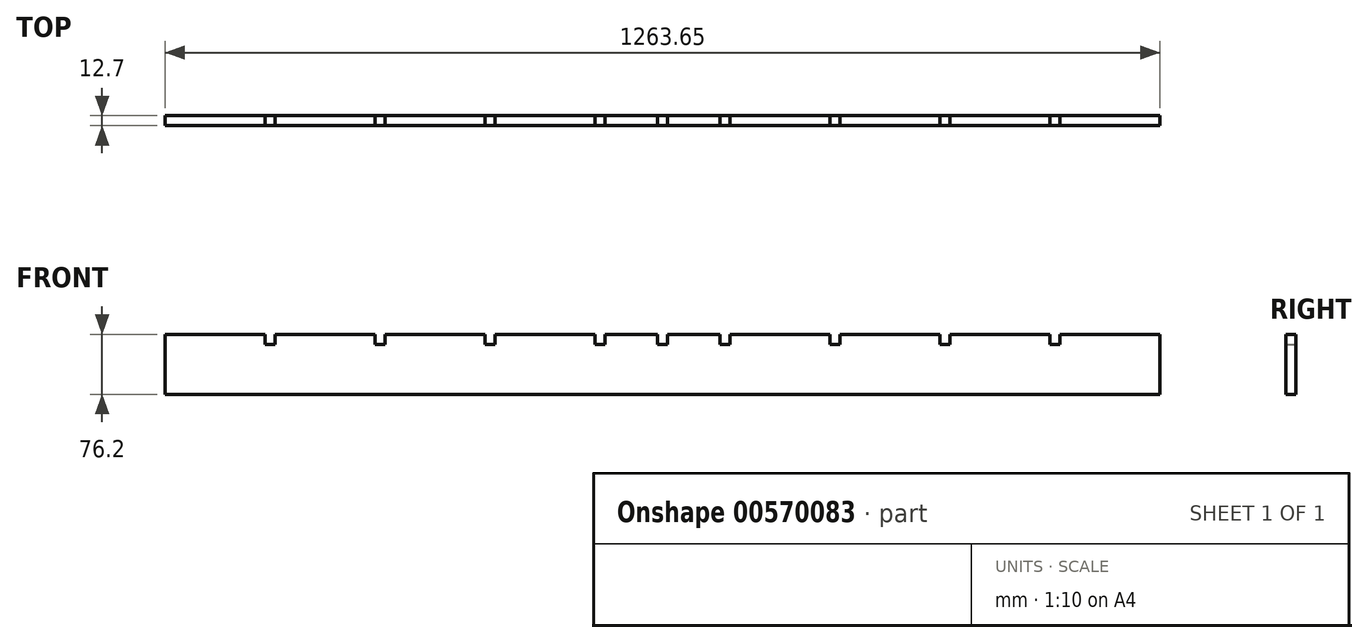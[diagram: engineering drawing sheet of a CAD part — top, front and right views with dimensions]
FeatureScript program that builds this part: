
annotation { "Feature Type Name" : "Feature", "Feature Type Description" : "" }
export const myFeature = defineFeature(function(context is Context, id is Id, definition is map)
    precondition{}
    {
        {
            var Q0;
            Q0=qCreatedBy(makeId("Right.planeOp"),FACE);
            var sketch = newSketch(context, id + "F0", { "sketchPlane" : qUnion([Q0])});
            skLineSegment(sketch, "E0", {"start": v(0, 0) * mm, "end": v(12.7, 0) * mm});
            skLineSegment(sketch, "E1", {"start": v(12.7, 0) * mm, "end": v(12.7, 76.2) * mm});
            skLineSegment(sketch, "E2", {"start": v(12.7, 76.2) * mm, "end": v(0, 76.2) * mm});
            skLineSegment(sketch, "E3", {"start": v(0, 76.2) * mm, "end": v(0, 0) * mm});
            skSolve(sketch);
        }
        {
            var Q0;
            Q0 = qSketchRegion(id + "F0", true);
            extrude(context, id + "F1", {"entities" : qUnion([Q0]), "oppositeDirection" : true, "depth" : 1263.65 * mm, "offsetDistance" : 25.4 * mm});
        }
        {
            var Q0;
            Q0=makeQuery(id+"F1.opExtrude","SWEPT_FACE",FACE,{"disambiguationData":[OSD([sQuery(id+"F0.wireOp",EDGE,"E1")])]});
            var sketch = newSketch(context, id + "F2", { "sketchPlane" : qUnion([Q0])});
            skLineSegment(sketch, "E4", {"start": v(127, 76.2) * mm, "end": v(127, 63.5) * mm});
            skLineSegment(sketch, "E5", {"start": v(127, 63.5) * mm, "end": v(139.7, 63.5) * mm});
            skLineSegment(sketch, "E6", {"start": v(139.7, 63.5) * mm, "end": v(139.7, 76.2) * mm});
            skLineSegment(sketch, "E7", {"start": v(1136.65, 76.2) * mm, "end": v(1136.65, 63.5) * mm});
            skLineSegment(sketch, "E8", {"start": v(1136.65, 63.5) * mm, "end": v(1123.95, 63.5) * mm});
            skLineSegment(sketch, "E9", {"start": v(1123.95, 63.5) * mm, "end": v(1123.95, 76.2) * mm});
            skLineSegment(sketch, "E10", {"start": v(996.95, 76.2) * mm, "end": v(996.95, 63.5) * mm});
            skLineSegment(sketch, "E11", {"start": v(996.95, 63.5) * mm, "end": v(984.25, 63.5) * mm});
            skLineSegment(sketch, "E12", {"start": v(984.25, 63.5) * mm, "end": v(984.25, 76.2) * mm});
            skLineSegment(sketch, "E13", {"start": v(266.7, 76.2) * mm, "end": v(266.7, 63.5) * mm});
            skLineSegment(sketch, "E14", {"start": v(266.7, 63.5) * mm, "end": v(279.4, 63.5) * mm});
            skLineSegment(sketch, "E15", {"start": v(279.4, 63.5) * mm, "end": v(279.4, 76.2) * mm});
            skLineSegment(sketch, "E16", {"start": v(406.4, 76.2) * mm, "end": v(406.4, 63.5) * mm});
            skLineSegment(sketch, "E17", {"start": v(406.4, 63.5) * mm, "end": v(419.1, 63.5) * mm});
            skLineSegment(sketch, "E18", {"start": v(419.1, 63.5) * mm, "end": v(419.1, 76.2) * mm});
            skLineSegment(sketch, "E19", {"start": v(857.25, 76.2) * mm, "end": v(857.25, 63.5) * mm});
            skLineSegment(sketch, "E20", {"start": v(857.25, 63.5) * mm, "end": v(844.55, 63.5) * mm});
            skLineSegment(sketch, "E21", {"start": v(844.55, 63.5) * mm, "end": v(844.55, 76.2) * mm});
            skLineSegment(sketch, "E22", {"start": v(546.1, 76.2) * mm, "end": v(546.1, 63.5) * mm});
            skLineSegment(sketch, "E23", {"start": v(546.1, 63.5) * mm, "end": v(558.8, 63.5) * mm});
            skLineSegment(sketch, "E24", {"start": v(558.8, 63.5) * mm, "end": v(558.8, 76.2) * mm});
            skLineSegment(sketch, "E25", {"start": v(717.55, 76.2) * mm, "end": v(717.55, 63.5) * mm});
            skLineSegment(sketch, "E26", {"start": v(717.55, 63.5) * mm, "end": v(704.85, 63.5) * mm});
            skLineSegment(sketch, "E27", {"start": v(704.85, 63.5) * mm, "end": v(704.85, 76.2) * mm});
            skSolve(sketch);
        }
        {
            var Q0;
            Q0 = qSketchRegion(id + "F2", true);
            var Q1;
            {var subQ0=sQuery(id+"F2.wireOp",EDGE,"E4");Q1=makeQuery(id+"F2.imprint","IMPRINT",FACE,{"disambiguationData":[TD([[makeQuery(id+"F2.imprint","IMPRINT",EDGE,{"derivedFrom":subQ0}),1.0]])]});}
            var Q2;
            {var subQ0=sQuery(id+"F2.wireOp",EDGE,"E13");Q2=makeQuery(id+"F2.imprint","IMPRINT",FACE,{"disambiguationData":[TD([[makeQuery(id+"F2.imprint","IMPRINT",EDGE,{"derivedFrom":subQ0}),1.0]])]});}
            var Q3;
            {var subQ0=sQuery(id+"F2.wireOp",EDGE,"E16");Q3=makeQuery(id+"F2.imprint","IMPRINT",FACE,{"disambiguationData":[TD([[makeQuery(id+"F2.imprint","IMPRINT",EDGE,{"derivedFrom":subQ0}),1.0]])]});}
            var Q4;
            {var subQ0=sQuery(id+"F2.wireOp",EDGE,"E22");Q4=makeQuery(id+"F2.imprint","IMPRINT",FACE,{"disambiguationData":[TD([[makeQuery(id+"F2.imprint","IMPRINT",EDGE,{"derivedFrom":subQ0}),1.0]])]});}
            var Q5;
            {var subQ0=sQuery(id+"F2.wireOp",EDGE,"E25");Q5=makeQuery(id+"F2.imprint","IMPRINT",FACE,{"disambiguationData":[TD([[makeQuery(id+"F2.imprint","IMPRINT",EDGE,{"derivedFrom":subQ0}),-1.0]])]});}
            var Q6;
            {var subQ0=sQuery(id+"F2.wireOp",EDGE,"E19");Q6=makeQuery(id+"F2.imprint","IMPRINT",FACE,{"disambiguationData":[TD([[makeQuery(id+"F2.imprint","IMPRINT",EDGE,{"derivedFrom":subQ0}),-1.0]])]});}
            var Q7;
            {var subQ0=sQuery(id+"F2.wireOp",EDGE,"E10");Q7=makeQuery(id+"F2.imprint","IMPRINT",FACE,{"disambiguationData":[TD([[makeQuery(id+"F2.imprint","IMPRINT",EDGE,{"derivedFrom":subQ0}),-1.0]])]});}
            var Q8;
            {var subQ0=sQuery(id+"F2.wireOp",EDGE,"E7");Q8=makeQuery(id+"F2.imprint","IMPRINT",FACE,{"disambiguationData":[TD([[makeQuery(id+"F2.imprint","IMPRINT",EDGE,{"derivedFrom":subQ0}),-1.0]])]});}
            extrude(context, id + "F3", {"entities" : qUnion([Q0, Q1, Q2, Q3, Q4, Q5, Q6, Q7, Q8]), "operationType" : NewBodyOperationType.REMOVE, "oppositeDirection" : true, "depth" : 12.7 * mm, "offsetDistance" : 25.4 * mm});
        }
        {
            var Q0;
            Q0=makeQuery(id+"F1.opExtrude","SWEPT_FACE",FACE,{"disambiguationData":[OSD([sQuery(id+"F0.wireOp",EDGE,"E1")])]});
            var sketch = newSketch(context, id + "F4", { "sketchPlane" : qUnion([Q0])});
            skLineSegment(sketch, "E28", {"start": v(625.48, 76.2) * mm, "end": v(625.48, 63.5) * mm});
            skLineSegment(sketch, "E29", {"start": v(625.48, 63.5) * mm, "end": v(638.18, 63.5) * mm});
            skLineSegment(sketch, "E30", {"start": v(638.18, 76.2) * mm, "end": v(638.18, 63.5) * mm});
            skLineSegment(sketch, "E31", {"start": v(631.83, 76.2) * mm, "end": v(682.62, 76.2) * mm});
            skLineSegment(sketch, "E32", {"start": v(631.83, 76.2) * mm, "end": v(581.03, 76.2) * mm});
            skSolve(sketch);
        }
        {
            var Q0;
            Q0 = qSketchRegion(id + "F4", true);
            var Q1;
            {var subQ0=sQuery(id+"F4.wireOp",EDGE,"LOQ7RS2L-H0Bv-9fxM-y4TT-2HombqMWhe3t");Q1=makeQuery(id+"F4.imprint","IMPRINT",FACE,{"disambiguationData":[TD([[makeQuery(id+"F4.imprint","IMPRINT",EDGE,{"derivedFrom":subQ0}),1.0]])]});}
            var Q2;
            {var subQ0=sQuery(id+"F4.wireOp",EDGE,"E28");Q2=makeQuery(id+"F4.imprint","IMPRINT",FACE,{"disambiguationData":[TD([[makeQuery(id+"F4.imprint","IMPRINT",EDGE,{"derivedFrom":subQ0}),1.0]])]});}
            extrude(context, id + "F5", {"entities" : qUnion([Q0, Q1, Q2]), "operationType" : NewBodyOperationType.REMOVE, "oppositeDirection" : true, "depth" : 12.7 * mm, "offsetDistance" : 25.4 * mm});
        }
    });
